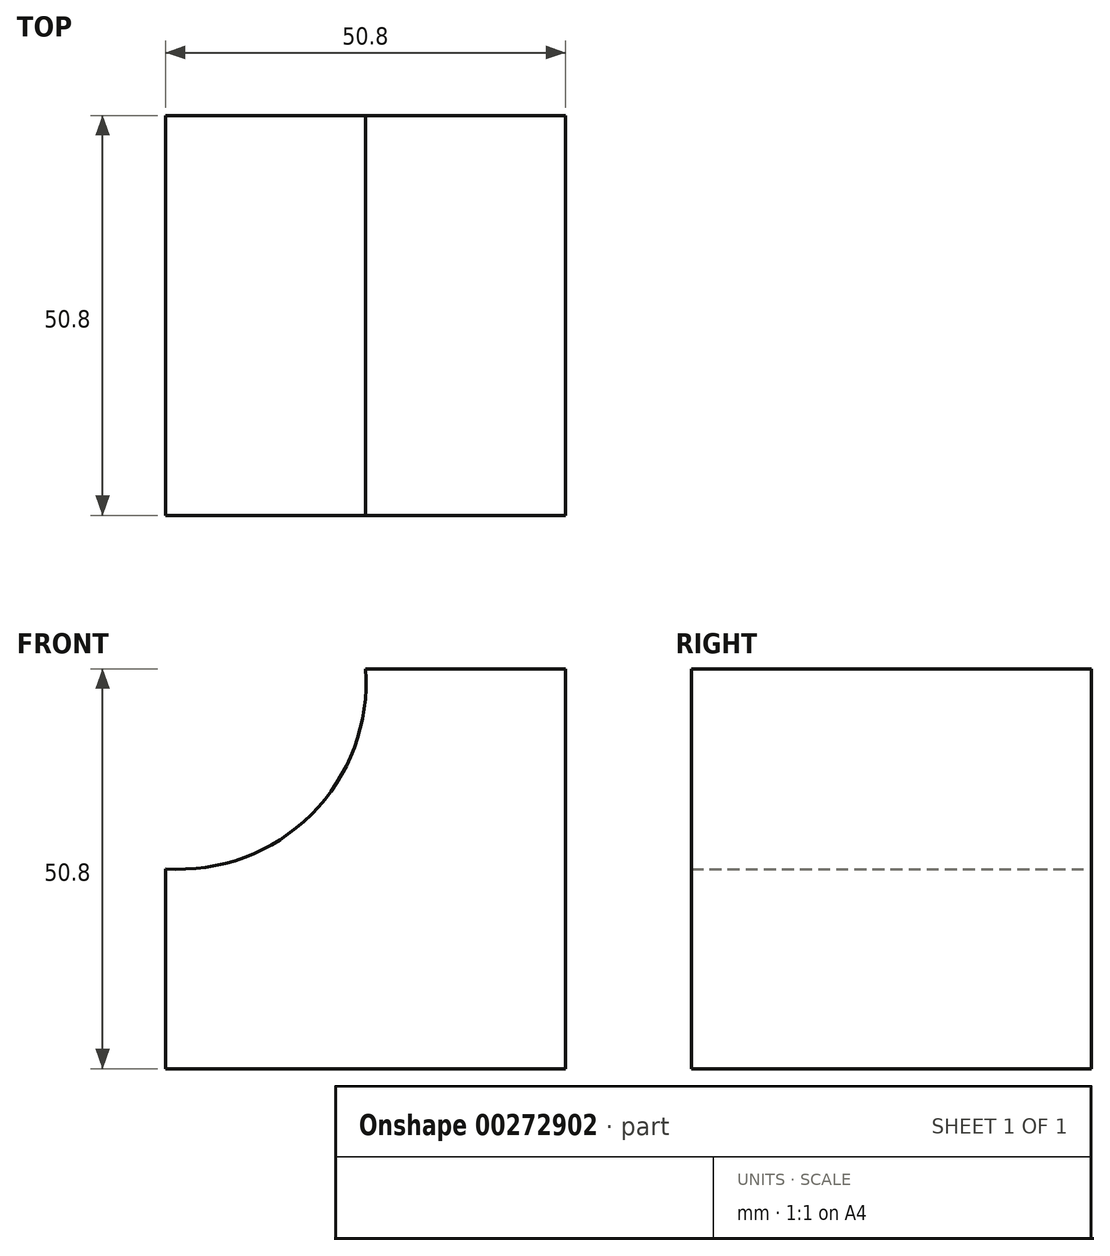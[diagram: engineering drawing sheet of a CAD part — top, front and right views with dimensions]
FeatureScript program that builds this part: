
annotation { "Feature Type Name" : "Feature", "Feature Type Description" : "" }
export const myFeature = defineFeature(function(context is Context, id is Id, definition is map)
    precondition{}
    {
        {
            var Q0;
            Q0=qCreatedBy(makeId("Front.planeOp"),FACE);
            var sketch = newSketch(context, id + "F0", { "sketchPlane" : qUnion([Q0])});
            skLineSegment(sketch, "E0", {"start": v(0, 0) * mm, "end": v(0, 50.8) * mm});
            skLineSegment(sketch, "E1", {"start": v(0, 50.8) * mm, "end": v(0, 0) * mm});
            skLineSegment(sketch, "E2", {"start": v(-50.8, 0) * mm, "end": v(0, 0) * mm});
            skLineSegment(sketch, "E3", {"start": v(-50.8, 0) * mm, "end": v(-50.8, 25.4) * mm});
            skLineSegment(sketch, "E4", {"start": v(0, 50.8) * mm, "end": v(-25.4, 50.8) * mm});
            skArc(sketch, "E5", {"start": v(-50.8, 25.4) * mm, "mid": v(-32.28, 32.28) * mm, "end": v(-25.4, 50.8) * mm});
            skSolve(sketch);
        }
        {
            var Q0;
            Q0 = qSketchRegion(id + "F0", true);
            extrude(context, id + "F1", {"entities" : qUnion([Q0]), "depth" : 50.8 * mm});
        }
    });
